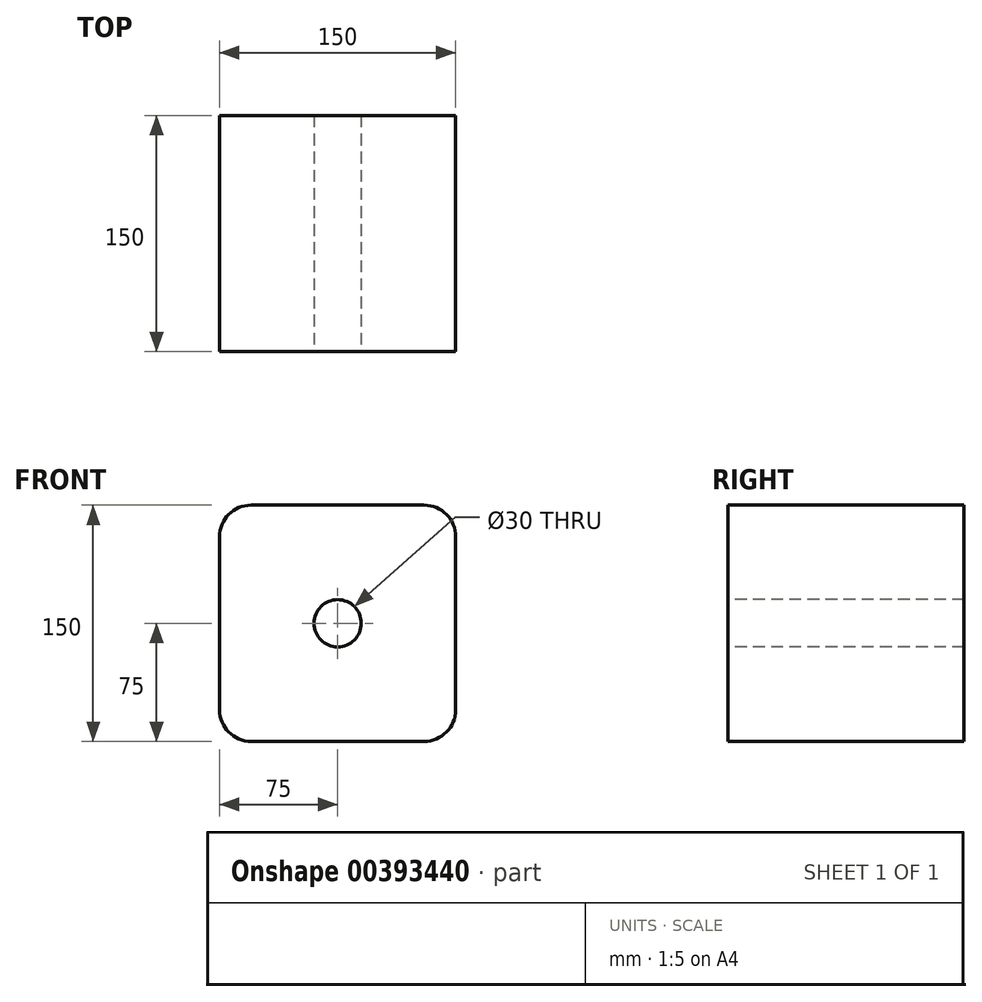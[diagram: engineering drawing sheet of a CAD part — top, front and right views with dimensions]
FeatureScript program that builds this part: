
annotation { "Feature Type Name" : "Feature", "Feature Type Description" : "" }
export const myFeature = defineFeature(function(context is Context, id is Id, definition is map)
    precondition{}
    {
        {
            var Q0;
            Q0=qCreatedBy(makeId("Front.planeOp"),FACE);
            var sketch = newSketch(context, id + "F0", { "sketchPlane" : qUnion([Q0])});
            skLineSegment(sketch, "E0.bottom", {"start": v(-55, 75) * mm, "end": v(55, 75) * mm});
            skLineSegment(sketch, "E0.top", {"start": v(-55, -75) * mm, "end": v(55, -75) * mm});
            skLineSegment(sketch, "E0.left", {"start": v(-75, 55) * mm, "end": v(-75, -55) * mm});
            skLineSegment(sketch, "E0.right", {"start": v(75, 55) * mm, "end": v(75, -55) * mm});
            skPoint(sketch, "E0.middle", {"position": v(0, 0) * mm});
            skPoint(sketch, "E1.visualSharp", {"position": v(75, 75) * mm});
            skArc(sketch, "E1.filletArc", {"start": v(75, 55) * mm, "mid": v(69.14, 69.14) * mm, "end": v(55, 75) * mm});
            skPoint(sketch, "E2.visualSharp", {"position": v(-75, 75) * mm});
            skArc(sketch, "E2.filletArc", {"start": v(-55, 75) * mm, "mid": v(-69.14, 69.14) * mm, "end": v(-75, 55) * mm});
            skPoint(sketch, "E3.visualSharp", {"position": v(75, -75) * mm});
            skArc(sketch, "E3.filletArc", {"start": v(55, -75) * mm, "mid": v(69.14, -69.14) * mm, "end": v(75, -55) * mm});
            skPoint(sketch, "E4.visualSharp", {"position": v(-75, -75) * mm});
            skArc(sketch, "E4.filletArc", {"start": v(-75, -55) * mm, "mid": v(-69.14, -69.14) * mm, "end": v(-55, -75) * mm});
            skSolve(sketch);
        }
        {
            var Q0;
            Q0 = qSketchRegion(id + "F0", true);
            extrude(context, id + "F1", {"entities" : qUnion([Q0]), "depth" : 150 * mm});
        }
        {
            var Q0;
            Q0=makeQuery(id+"F1.opExtrude","CAP_FACE",FACE,{"disambiguationData":[OSD([sQuery(id+"F0.wireOp",EDGE,"E0.bottom"),sQuery(id+"F0.wireOp",EDGE,"E0.top"),sQuery(id+"F0.wireOp",EDGE,"E0.left"),sQuery(id+"F0.wireOp",EDGE,"E0.right"),sQuery(id+"F0.wireOp",EDGE,"E1.filletArc"),sQuery(id+"F0.wireOp",EDGE,"E2.filletArc"),sQuery(id+"F0.wireOp",EDGE,"E3.filletArc"),sQuery(id+"F0.wireOp",EDGE,"E4.filletArc")])],"isStart":false});
            var sketch = newSketch(context, id + "F2", { "sketchPlane" : qUnion([Q0])});
            skCircle(sketch, "E5", {"center": v(0, 0) * mm, "radius": 15 * mm});
            skSolve(sketch);
        }
        {
            var Q0;
            Q0 = qSketchRegion(id + "F2", true);
            extrude(context, id + "F3", {"entities" : qUnion([Q0]), "operationType" : NewBodyOperationType.REMOVE, "endBound" : BoundingType.THROUGH_ALL, "oppositeDirection" : true, "depth" : 25.4 * mm});
        }
    });
